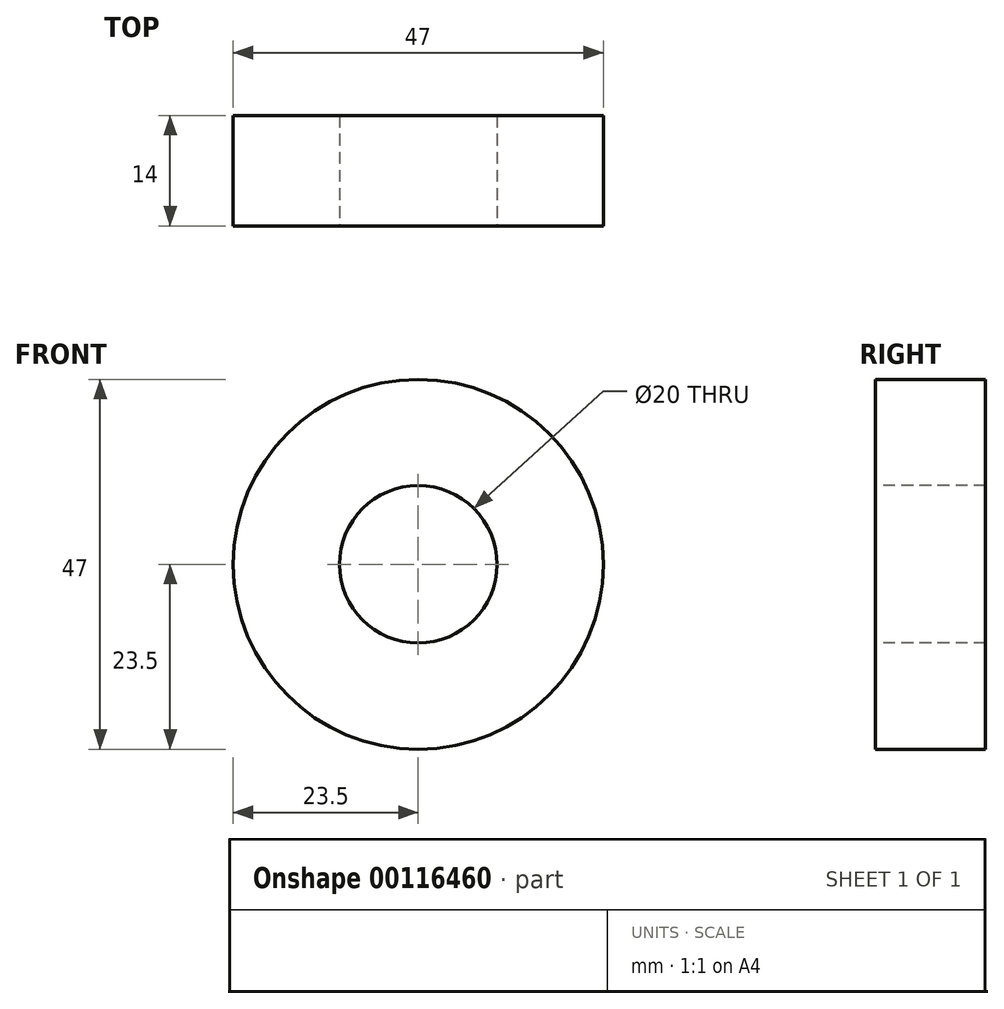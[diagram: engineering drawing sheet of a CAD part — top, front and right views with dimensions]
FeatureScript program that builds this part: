
annotation { "Feature Type Name" : "Feature", "Feature Type Description" : "" }
export const myFeature = defineFeature(function(context is Context, id is Id, definition is map)
    precondition{}
    {
        {
            var Q0;
            Q0=qCreatedBy(makeId("Front.planeOp"),FACE);
            var sketch = newSketch(context, id + "F0", { "sketchPlane" : qUnion([Q0])});
            skCircle(sketch, "E0", {"center": v(0, 0) * mm, "radius": 10 * mm});
            skCircle(sketch, "E1", {"center": v(0, 0) * mm, "radius": 23.5 * mm});
            skSolve(sketch);
        }
        {
            var Q0;
            Q0=makeQuery(id+"F0.imprint","IMPRINT",FACE,{"disambiguationData":[TD([[makeQuery(id+"F0.imprint","IMPRINT",EDGE,{"derivedFrom":sQuery(id+"F0.wireOp",EDGE,"E0")}),-1.0]])]});
            extrude(context, id + "F1", {"entities" : qUnion([Q0]), "oppositeDirection" : true, "depth" : 14 * mm});
        }
    });
